# Revit family: Kosz_na_smieci_z_pokrywa_wiszacy_50 l
name_source: partatom
category: Furniture
units: mm (PartAtom-declared; Revit-internal decimal feet)

## family parameters
Always vertical = Yes
Cut with Voids When Loaded = No
Host = Wall
Room Calculation Point = No
Shared = No

## types (1)
- WB50S
    Depth / Glebokosc = 220 mm  [stored 0.721785 ft]
    Description = Kosz na śmieci z pokrywą uchylną to bardzo pojemny model. Wykonany jest z stali nierdzewnej matowej, która nadaje mu dużą odporność na uszkodzenia oraz elegancki wygląd. Pojemnik na odpady w prosty sposób montowany jest na ścianie. Równie łatwo czyści się go i konserwuje. Dzięki uchylnej pokrywie, zasłaniającej wnętrze kosza, zapewnia on wysoki poziom higieny. Polecany jest do toalet publicznych o wysokim natężeniu ruchu.
    Height / Wysokosc = 700 mm  [stored 2.29659 ft]
    Manufacturer = FANECO.com
    Manufacturer code / Kod producenta = 5901764292159
    Material = Stal nierdzewna szczotkowana
    Material finish / Wykonczenie = Stal nierdzewna 430 szczotkowana
    Product code / Kod produktu = WB50S
    Type Comments = Kosz na śmieci z pokrywą wiszący 50 l stal szlachetna matowa
    URL = https://faneco.com
    Weight / Waga = 7 kg
    Width / Szerokosc = 400 mm  [stored 1.31234 ft]

note: [stored X ft] marks values corroborated as IEEE doubles in the binary element streams (Revit-internal decimal feet)

## geometry (parser evidence)
native form markers: Sweep x12
no freeform markers — native parametric forms only
